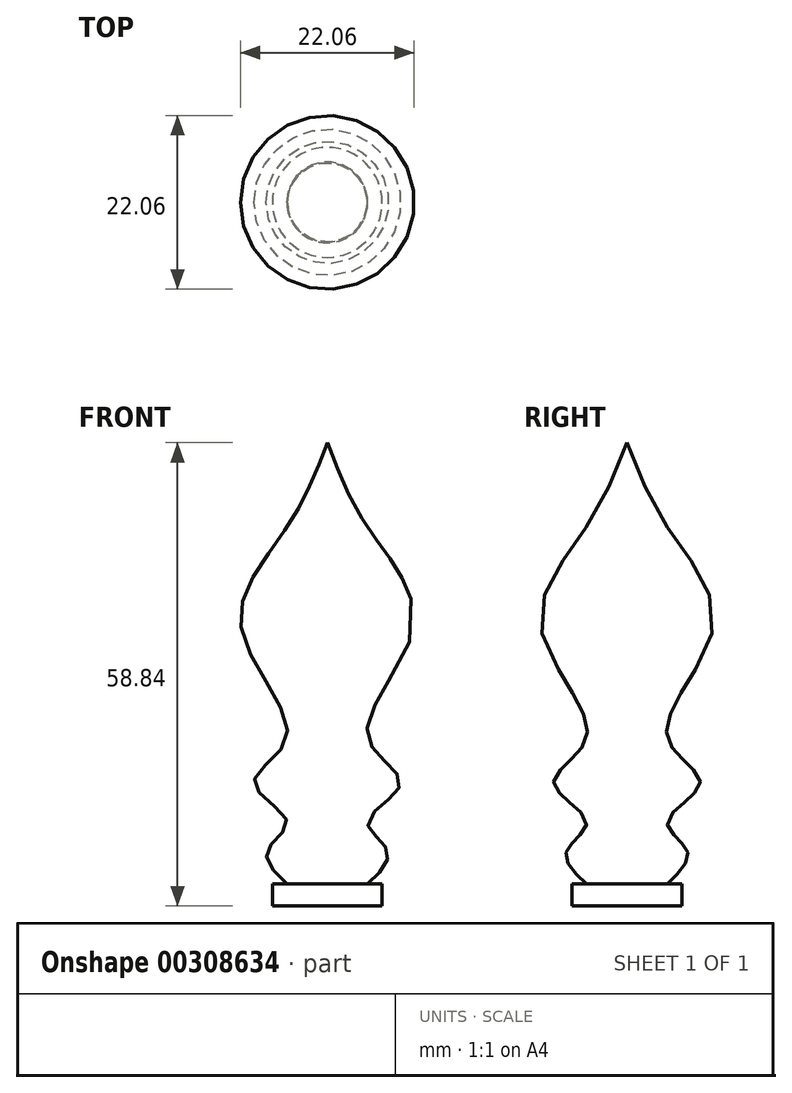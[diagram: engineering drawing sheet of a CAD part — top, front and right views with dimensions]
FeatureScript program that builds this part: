
annotation { "Feature Type Name" : "Feature", "Feature Type Description" : "" }
export const myFeature = defineFeature(function(context is Context, id is Id, definition is map)
    precondition{}
    {
        {
            var Q0;
            Q0=qCreatedBy(makeId("Front.planeOp"),FACE);
            var sketch = newSketch(context, id + "F0", { "sketchPlane" : qUnion([Q0])});
            skLineSegment(sketch, "E0", {"start": v(0, 29.77) * mm, "end": v(0, -29.07) * mm});
            skLineSegment(sketch, "E1", {"start": v(0, -29.07) * mm, "end": v(-6.98, -29.07) * mm});
            skLineSegment(sketch, "E2", {"start": v(-6.98, -29.07) * mm, "end": v(-6.98, -26.28) * mm});
            skLineSegment(sketch, "E3", {"start": v(-6.98, -26.28) * mm, "end": v(-5.12, -26.28) * mm});
            skFitSpline(sketch, "E4", {"points": [v(-5.12, -26.28) * mm, v(-7.68, -22.1) * mm, v(-5.12, -18.37) * mm, v(-9.3, -13.5) * mm, v(-5.12, -7.68) * mm, v(-10.93, 6.28) * mm, v(-5.12, 19.07) * mm, v(0, 29.77) * mm], "startDerivative": vector(-42.41, 40.04) * mm, "endDerivative": vector(24.12, 63.34) * mm});
            skSolve(sketch);
        }
        {
            var Q0;
            Q0 = qSketchRegion(id + "F0", true);
            var Q1;
            Q1=sQuery(id+"F0.wireOp",EDGE,"E0");
            revolve(context, id + "F1", {"entities" : qUnion([Q0]), "axis" : qUnion([Q1]), "revolveType" : RevolveType.FULL});
        }
    });
